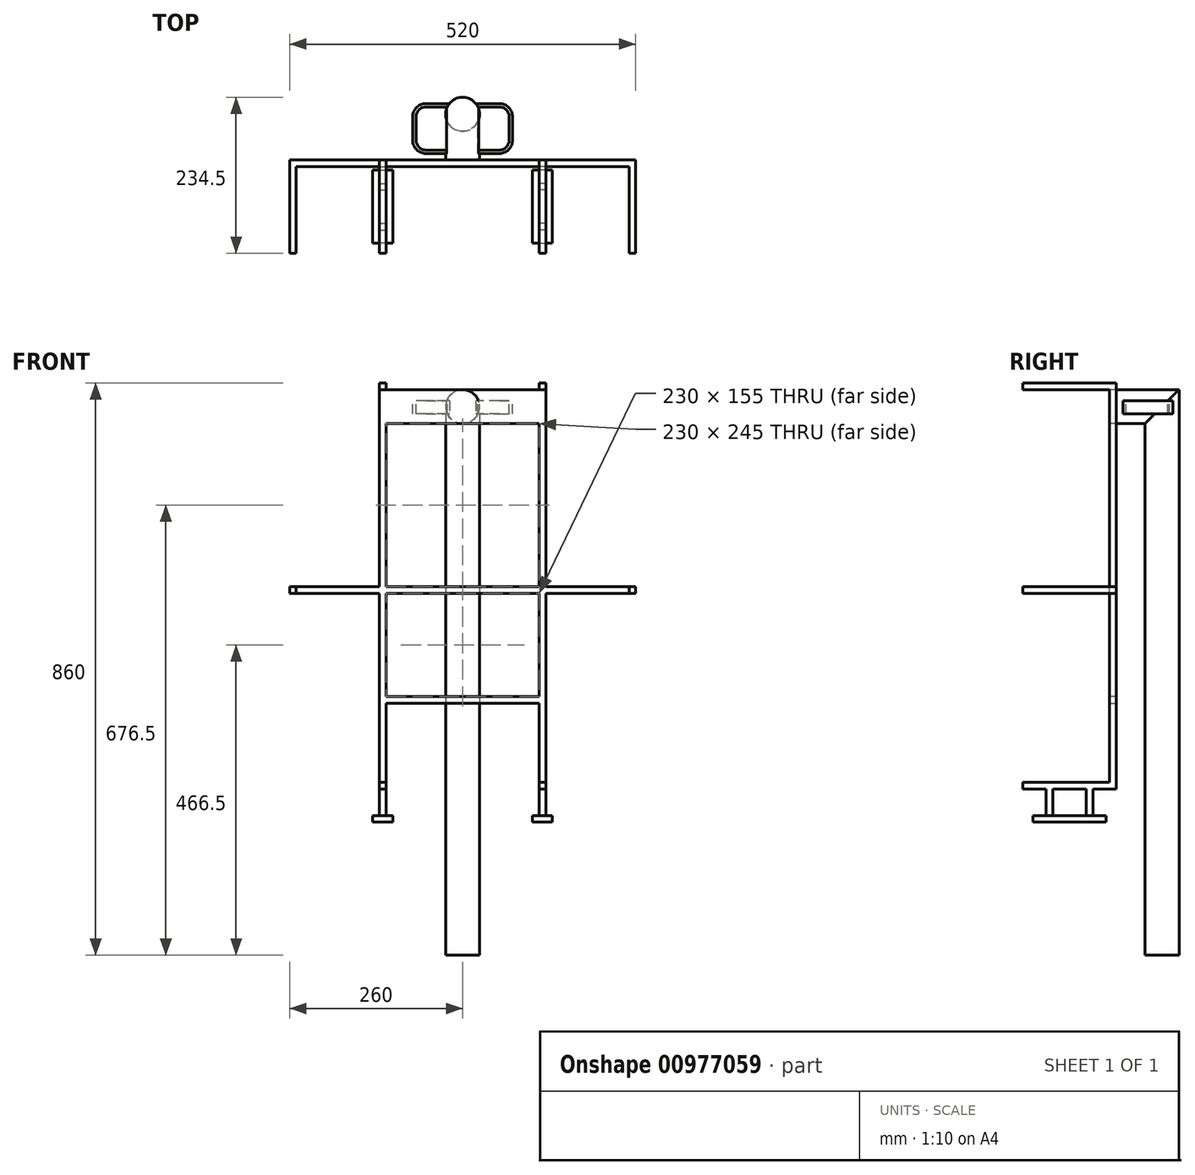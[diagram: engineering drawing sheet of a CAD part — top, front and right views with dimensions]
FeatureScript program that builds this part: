
annotation { "Feature Type Name" : "Feature", "Feature Type Description" : "" }
export const myFeature = defineFeature(function(context is Context, id is Id, definition is map)
    precondition{}
    {
        {
            var Q0;
            Q0=qCreatedBy(makeId("Top.planeOp"),FACE);
            var sketch = newSketch(context, id + "F0", { "sketchPlane" : qUnion([Q0])});
            skCircle(sketch, "E0", {"center": v(0, 0) * mm, "radius": 25.5 * mm});
            skSolve(sketch);
        }
        {
            var Q0;
            Q0=makeQuery(id+"F0.imprint","IMPRINT",FACE,{"disambiguationData":[TD([[makeQuery(id+"F0.imprint","IMPRINT",EDGE,{"derivedFrom":sQuery(id+"F0.wireOp",EDGE,"E0")}),1.0]])]});
            extrude(context, id + "F1", {"entities" : qUnion([Q0]), "depth" : 850 * mm, "offsetDistance" : 25 * mm});
        }
        {
            var Q0;
            Q0=qCreatedBy(makeId("Front.planeOp"),FACE);
            var sketch = newSketch(context, id + "F2", { "sketchPlane" : qUnion([Q0])});
            skCircle(sketch, "E1", {"center": v(0, 824.5) * mm, "radius": 25.5 * mm});
            skSolve(sketch);
        }
        {
            var Q0;
            Q0=makeQuery(id+"F2.imprint","IMPRINT",FACE,{"disambiguationData":[TD([[makeQuery(id+"F2.imprint","IMPRINT",EDGE,{"derivedFrom":sQuery(id+"F2.wireOp",EDGE,"E1")}),1.0]])]});
            extrude(context, id + "F3", {"entities" : qUnion([Q0]), "operationType" : NewBodyOperationType.ADD, "depth" : 69 * mm, "offsetDistance" : 25 * mm});
        }
        {
            var Q0;
            Q0=makeQuery(id+"F3.opExtrude","CAP_FACE",FACE,{"disambiguationData":[OSD([sQuery(id+"F2.wireOp",EDGE,"E1")])],"isStart":false});
            var sketch = newSketch(context, id + "F4", { "sketchPlane" : qUnion([Q0])});
            skArc(sketch, "E2", {"start": v(25.5, 824.5) * mm, "mid": v(0, 850) * mm, "end": v(-25.5, 824.5) * mm});
            skLineSegment(sketch, "E3", {"start": v(-25.5, 824.5) * mm, "end": v(-40.8, 824.5) * mm});
            skLineSegment(sketch, "E4", {"start": v(-40.8, 824.5) * mm, "end": v(-40.8, 859.7) * mm});
            skLineSegment(sketch, "E5", {"start": v(-40.8, 859.7) * mm, "end": v(45.6, 859.7) * mm});
            skLineSegment(sketch, "E6", {"start": v(45.6, 859.7) * mm, "end": v(45.6, 824.5) * mm});
            skLineSegment(sketch, "E7", {"start": v(45.6, 824.5) * mm, "end": v(25.5, 824.5) * mm});
            skSolve(sketch);
        }
        {
            var Q0;
            Q0=makeQuery(id+"F4.imprint","IMPRINT",FACE,{"disambiguationData":[TD([[makeQuery(id+"F4.imprint","IMPRINT",EDGE,{"derivedFrom":sQuery(id+"F4.wireOp",EDGE,"E2")}),-1.0]])]});
            extrude(context, id + "F5", {"entities" : qUnion([Q0]), "operationType" : NewBodyOperationType.REMOVE, "oppositeDirection" : true, "depth" : 150 * mm, "offsetDistance" : 25 * mm});
        }
        {
            var Q0;
            Q0=qCreatedBy(makeId("Right.planeOp"),FACE);
            var sketch = newSketch(context, id + "F6", { "sketchPlane" : qUnion([Q0])});
            skLineSegment(sketch, "E8", {"start": v(-59, 823.42) * mm, "end": v(-59, 833.42) * mm});
            skLineSegment(sketch, "E9", {"start": v(-59, 833.42) * mm, "end": v(16, 833.42) * mm});
            skLineSegment(sketch, "E10", {"start": v(16, 833.42) * mm, "end": v(16, 813.42) * mm});
            skLineSegment(sketch, "E11", {"start": v(16, 813.42) * mm, "end": v(-59, 813.42) * mm});
            skLineSegment(sketch, "E12", {"start": v(-59, 813.42) * mm, "end": v(-59, 823.42) * mm});
            skSolve(sketch);
        }
        {
            var Q0;
            Q0 = qSketchRegion(id + "F6", true);
            extrude(context, id + "F7", {"entities" : qUnion([Q0]), "operationType" : NewBodyOperationType.ADD, "endBound" : BoundingType.SYMMETRIC, "depth" : 150 * mm, "offsetDistance" : 25 * mm});
        }
        {
            var Q0;
            Q0=makeQuery(id+"F7.opExtrude","CAP_EDGE",EDGE,{"disambiguationData":[OSD([sQuery(id+"F6.wireOp",EDGE,"E10")])],"isStart":false});
            var Q1;
            Q1=makeQuery(id+"F7.opExtrude","CAP_EDGE",EDGE,{"disambiguationData":[OSD([sQuery(id+"F6.wireOp",EDGE,"E10")])],"isStart":true});
            var Q2;
            Q2=makeQuery(id+"F7.opExtrude","CAP_EDGE",EDGE,{"disambiguationData":[OSD([sQuery(id+"F6.wireOp",EDGE,"E8"),sQuery(id+"F6.wireOp",EDGE,"E12")])],"isStart":true});
            var Q3;
            Q3=makeQuery(id+"F7.opExtrude","CAP_EDGE",EDGE,{"disambiguationData":[OSD([sQuery(id+"F6.wireOp",EDGE,"E8"),sQuery(id+"F6.wireOp",EDGE,"E12")])],"isStart":false});
            fillet(context, id + "F8", {"entities" : qUnion([Q0, Q1, Q2, Q3]), "radius" : 20 * mm, "tangentPropagation" : true, "allowEdgeOverflow" : false});
        }
        {
            var Q0;
            {var subQ0=sQuery(id+"F6.wireOp",EDGE,"E12");var subQ1=sQuery(id+"F6.wireOp",EDGE,"E10");var subQ2=sQuery(id+"F6.wireOp",EDGE,"E9");var subQ3=sQuery(id+"F6.wireOp",EDGE,"E8");Q0=makeQuery(id+"F7.boolean.opBoolean","SPLIT",FACE,{"disambiguationData":[TD([makeQuery(id+"F7.opExtrude","CAP_FACE",FACE,{"disambiguationData":[OSD([subQ3,subQ2,subQ1,sQuery(id+"F6.wireOp",EDGE,"E11"),subQ0])],"isStart":false})])],"derivedFrom":makeQuery(id+"F7.opExtrude","SWEPT_FACE",FACE,{"disambiguationData":[OSD([subQ2])]})});}
            var sketch = newSketch(context, id + "F9", { "sketchPlane" : qUnion([Q0])});
            skLineSegment(sketch, "E13", {"start": v(23.89, -54) * mm, "end": v(55, -54) * mm});
            skLineSegment(sketch, "E14", {"start": v(55, 11) * mm, "end": v(23, 11) * mm});
            skLineSegment(sketch, "E15", {"start": v(70, -4) * mm, "end": v(70, -39) * mm});
            skArc(sketch, "E16", {"start": v(55, -54) * mm, "mid": v(65.6, -49.6) * mm, "end": v(70, -39) * mm});
            skArc(sketch, "E17", {"start": v(70, -4) * mm, "mid": v(65.6, 6.6) * mm, "end": v(55, 11) * mm});
            skLineSegment(sketch, "E18", {"start": v(23.89, -54) * mm, "end": v(23.89, 8.92) * mm});
            skLineSegment(sketch, "E19", {"start": v(23.89, 8.92) * mm, "end": v(23, 11) * mm});
            skLineSegment(sketch, "E20.MirrorCS", {"start": v(-23.89, 8.92) * mm, "end": v(-23, 11) * mm});
            skLineSegment(sketch, "E21.MirrorCS", {"start": v(-23.89, -54) * mm, "end": v(-23.89, 8.92) * mm});
            skLineSegment(sketch, "E22.MirrorCS", {"start": v(-55, 11) * mm, "end": v(-23, 11) * mm});
            skArc(sketch, "E23.MirrorCS", {"start": v(-70, -4) * mm, "mid": v(-65.6, 6.6) * mm, "end": v(-55, 11) * mm});
            skLineSegment(sketch, "E24.MirrorCS", {"start": v(-23.89, -54) * mm, "end": v(-55, -54) * mm});
            skLineSegment(sketch, "E25.MirrorCS", {"start": v(-70, -4) * mm, "end": v(-70, -39) * mm});
            skArc(sketch, "E26.MirrorCS", {"start": v(-55, -54) * mm, "mid": v(-65.6, -49.6) * mm, "end": v(-70, -39) * mm});
            skSolve(sketch);
        }
        {
            var Q0;
            Q0=makeQuery(id+"F9.imprint","IMPRINT",FACE,{"disambiguationData":[TD([[makeQuery(id+"F9.imprint","IMPRINT",EDGE,{"derivedFrom":sQuery(id+"F9.wireOp",EDGE,"E20.MirrorCS")}),1.0]])]});
            var Q1;
            Q1=makeQuery(id+"F9.imprint","IMPRINT",FACE,{"disambiguationData":[TD([[makeQuery(id+"F9.imprint","IMPRINT",EDGE,{"derivedFrom":sQuery(id+"F9.wireOp",EDGE,"E13")}),1.0]])]});
            extrude(context, id + "F10", {"entities" : qUnion([Q0, Q1]), "operationType" : NewBodyOperationType.REMOVE, "oppositeDirection" : true, "depth" : 20 * mm, "offsetDistance" : 25 * mm});
        }
        {
            var Q0;
            Q0=makeQuery(id+"F3.opExtrude","CAP_FACE",FACE,{"disambiguationData":[OSD([sQuery(id+"F2.wireOp",EDGE,"E1")])],"isStart":false});
            var sketch = newSketch(context, id + "F11", { "sketchPlane" : qUnion([Q0])});
            skLineSegment(sketch, "E27", {"start": v(125, 850) * mm, "end": v(125, 554) * mm});
            skLineSegment(sketch, "E28", {"start": v(125, 250) * mm, "end": v(115, 250) * mm});
            skLineSegment(sketch, "E29", {"start": v(260, 544) * mm, "end": v(260, 554) * mm});
            skLineSegment(sketch, "E30", {"start": v(260, 554) * mm, "end": v(125, 554) * mm});
            skLineSegment(sketch, "E31.trimOffspring", {"start": v(125, 544) * mm, "end": v(125, 250) * mm});
            skLineSegment(sketch, "E32.trimOffspring", {"start": v(125, 544) * mm, "end": v(260, 544) * mm});
            skLineSegment(sketch, "E33", {"start": v(0, 379) * mm, "end": v(115, 379) * mm});
            skLineSegment(sketch, "E34.trimOffspring", {"start": v(115, 379) * mm, "end": v(115, 250) * mm});
            skLineSegment(sketch, "E35.MirrorCS", {"start": v(-125, 250) * mm, "end": v(-115, 250) * mm});
            skLineSegment(sketch, "E36.MirrorCS", {"start": v(0, 379) * mm, "end": v(-115, 379) * mm});
            skLineSegment(sketch, "E37.MirrorCS", {"start": v(-115, 379) * mm, "end": v(-115, 250) * mm});
            skLineSegment(sketch, "E38.MirrorCS", {"start": v(-260, 544) * mm, "end": v(-260, 554) * mm});
            skLineSegment(sketch, "E39.MirrorCS", {"start": v(-125, 544) * mm, "end": v(-125, 250) * mm});
            skLineSegment(sketch, "E40.MirrorCS", {"start": v(-260, 554) * mm, "end": v(-125, 554) * mm});
            skLineSegment(sketch, "E41.MirrorCS", {"start": v(-125, 544) * mm, "end": v(-260, 544) * mm});
            skLineSegment(sketch, "E42.MirrorCS", {"start": v(-125, 850) * mm, "end": v(-125, 554) * mm});
            skLineSegment(sketch, "E43", {"start": v(-125, 850) * mm, "end": v(125, 850) * mm});
            skSolve(sketch);
        }
        {
            var Q0;
            Q0 = qSketchRegion(id + "F11", true);
            extrude(context, id + "F12", {"entities" : qUnion([Q0]), "depth" : 10 * mm, "offsetDistance" : 25 * mm});
        }
        {
            var Q0;
            Q0=makeQuery(id+"F12.opExtrude","CAP_FACE",FACE,{"disambiguationData":[OSD([sQuery(id+"F11.wireOp",EDGE,"E27"),sQuery(id+"F11.wireOp",EDGE,"E28"),sQuery(id+"F11.wireOp",EDGE,"E29"),sQuery(id+"F11.wireOp",EDGE,"E30"),sQuery(id+"F11.wireOp",EDGE,"E31.trimOffspring"),sQuery(id+"F11.wireOp",EDGE,"E32.trimOffspring"),sQuery(id+"F11.wireOp",EDGE,"E33"),sQuery(id+"F11.wireOp",EDGE,"E34.trimOffspring"),sQuery(id+"F11.wireOp",EDGE,"E35.MirrorCS"),sQuery(id+"F11.wireOp",EDGE,"E36.MirrorCS"),sQuery(id+"F11.wireOp",EDGE,"E37.MirrorCS"),sQuery(id+"F11.wireOp",EDGE,"E38.MirrorCS"),sQuery(id+"F11.wireOp",EDGE,"E39.MirrorCS"),sQuery(id+"F11.wireOp",EDGE,"E40.MirrorCS"),sQuery(id+"F11.wireOp",EDGE,"E41.MirrorCS"),sQuery(id+"F11.wireOp",EDGE,"E42.MirrorCS"),sQuery(id+"F11.wireOp",EDGE,"E43")])],"isStart":false});
            var sketch = newSketch(context, id + "F13", { "sketchPlane" : qUnion([Q0])});
            skLineSegment(sketch, "E44", {"start": v(0, 799) * mm, "end": v(115, 799) * mm});
            skLineSegment(sketch, "E45", {"start": v(115, 799) * mm, "end": v(115, 554) * mm});
            skLineSegment(sketch, "E46", {"start": v(0, 799) * mm, "end": v(-115, 799) * mm});
            skLineSegment(sketch, "E47", {"start": v(-115, 799) * mm, "end": v(-115, 554) * mm});
            skLineSegment(sketch, "E48", {"start": v(-115, 554) * mm, "end": v(115, 554) * mm});
            skLineSegment(sketch, "E49", {"start": v(-115, 544) * mm, "end": v(115, 544) * mm});
            skLineSegment(sketch, "E50", {"start": v(115, 544) * mm, "end": v(115, 389) * mm});
            skLineSegment(sketch, "E51", {"start": v(115, 389) * mm, "end": v(-115, 389) * mm});
            skLineSegment(sketch, "E52", {"start": v(-115, 389) * mm, "end": v(-115, 544) * mm});
            skSolve(sketch);
        }
        {
            var Q0;
            Q0=makeQuery(id+"F13.imprint","IMPRINT",FACE,{"disambiguationData":[TD([[makeQuery(id+"F13.imprint","IMPRINT",EDGE,{"derivedFrom":sQuery(id+"F13.wireOp",EDGE,"E44")}),-1.0]])]});
            var Q1;
            Q1=makeQuery(id+"F13.imprint","IMPRINT",FACE,{"disambiguationData":[TD([[makeQuery(id+"F13.imprint","IMPRINT",EDGE,{"derivedFrom":sQuery(id+"F13.wireOp",EDGE,"E49")}),-1.0]])]});
            extrude(context, id + "F14", {"entities" : qUnion([Q0, Q1]), "operationType" : NewBodyOperationType.REMOVE, "oppositeDirection" : true, "depth" : 10 * mm, "offsetDistance" : 25 * mm});
        }
        {
            var Q0;
            Q0=makeQuery(id+"F12.opExtrude","CAP_FACE",FACE,{"disambiguationData":[OSD([sQuery(id+"F11.wireOp",EDGE,"E27"),sQuery(id+"F11.wireOp",EDGE,"E28"),sQuery(id+"F11.wireOp",EDGE,"E29"),sQuery(id+"F11.wireOp",EDGE,"E30"),sQuery(id+"F11.wireOp",EDGE,"E31.trimOffspring"),sQuery(id+"F11.wireOp",EDGE,"E32.trimOffspring"),sQuery(id+"F11.wireOp",EDGE,"E33"),sQuery(id+"F11.wireOp",EDGE,"E34.trimOffspring"),sQuery(id+"F11.wireOp",EDGE,"E35.MirrorCS"),sQuery(id+"F11.wireOp",EDGE,"E36.MirrorCS"),sQuery(id+"F11.wireOp",EDGE,"E37.MirrorCS"),sQuery(id+"F11.wireOp",EDGE,"E38.MirrorCS"),sQuery(id+"F11.wireOp",EDGE,"E39.MirrorCS"),sQuery(id+"F11.wireOp",EDGE,"E40.MirrorCS"),sQuery(id+"F11.wireOp",EDGE,"E41.MirrorCS"),sQuery(id+"F11.wireOp",EDGE,"E42.MirrorCS"),sQuery(id+"F11.wireOp",EDGE,"E43")])],"isStart":false});
            var sketch = newSketch(context, id + "F15", { "sketchPlane" : qUnion([Q0])});
            skLineSegment(sketch, "E53.bottom", {"start": v(-260, 554) * mm, "end": v(-250, 554) * mm});
            skLineSegment(sketch, "E53.top", {"start": v(-260, 544) * mm, "end": v(-250, 544) * mm});
            skLineSegment(sketch, "E53.left", {"start": v(-260, 554) * mm, "end": v(-260, 544) * mm});
            skLineSegment(sketch, "E53.right", {"start": v(-250, 554) * mm, "end": v(-250, 544) * mm});
            skLineSegment(sketch, "E54.bottom", {"start": v(260, 544) * mm, "end": v(250, 544) * mm});
            skLineSegment(sketch, "E54.top", {"start": v(260, 554) * mm, "end": v(250, 554) * mm});
            skLineSegment(sketch, "E54.left", {"start": v(260, 544) * mm, "end": v(260, 554) * mm});
            skLineSegment(sketch, "E54.right", {"start": v(250, 544) * mm, "end": v(250, 554) * mm});
            skLineSegment(sketch, "E55.bottom", {"start": v(-115, 250) * mm, "end": v(-125, 250) * mm});
            skLineSegment(sketch, "E55.top", {"start": v(-115, 260) * mm, "end": v(-125, 260) * mm});
            skLineSegment(sketch, "E55.left", {"start": v(-115, 250) * mm, "end": v(-115, 260) * mm});
            skLineSegment(sketch, "E55.right", {"start": v(-125, 250) * mm, "end": v(-125, 260) * mm});
            skLineSegment(sketch, "E56.bottom", {"start": v(125, 250) * mm, "end": v(115, 250) * mm});
            skLineSegment(sketch, "E56.top", {"start": v(125, 260) * mm, "end": v(115, 260) * mm});
            skLineSegment(sketch, "E56.left", {"start": v(125, 250) * mm, "end": v(125, 260) * mm});
            skLineSegment(sketch, "E56.right", {"start": v(115, 250) * mm, "end": v(115, 260) * mm});
            skSolve(sketch);
        }
        {
            var Q0;
            Q0=makeQuery(id+"F12.opExtrude","SWEPT_FACE",FACE,{"disambiguationData":[OSD([sQuery(id+"F11.wireOp",EDGE,"E43")])]});
            var sketch = newSketch(context, id + "F16", { "sketchPlane" : qUnion([Q0])});
            skLineSegment(sketch, "E57.bottom", {"start": v(-125, -69) * mm, "end": v(-115, -69) * mm});
            skLineSegment(sketch, "E57.top", {"start": v(-125, -209) * mm, "end": v(-115, -209) * mm});
            skLineSegment(sketch, "E57.left", {"start": v(-125, -69) * mm, "end": v(-125, -209) * mm});
            skLineSegment(sketch, "E57.right", {"start": v(-115, -69) * mm, "end": v(-115, -209) * mm});
            skLineSegment(sketch, "E58.bottom", {"start": v(125, -69) * mm, "end": v(115, -69) * mm});
            skLineSegment(sketch, "E58.top", {"start": v(125, -209) * mm, "end": v(115, -209) * mm});
            skLineSegment(sketch, "E58.left", {"start": v(125, -69) * mm, "end": v(125, -209) * mm});
            skLineSegment(sketch, "E58.right", {"start": v(115, -69) * mm, "end": v(115, -209) * mm});
            skSolve(sketch);
        }
        {
            var Q0;
            {var subQ0=sQuery(id+"F16.wireOp",EDGE,"E57.top");Q0=makeQuery(id+"F16.imprint","IMPRINT",FACE,{"disambiguationData":[TD([[makeQuery(id+"F16.imprint","IMPRINT",EDGE,{"derivedFrom":subQ0}),1.0]])]});}
            var Q1;
            {var subQ0=sQuery(id+"F16.wireOp",EDGE,"E58.bottom");Q1=makeQuery(id+"F16.imprint","IMPRINT",FACE,{"disambiguationData":[TD([[makeQuery(id+"F16.imprint","IMPRINT",EDGE,{"derivedFrom":subQ0}),-1.0]])]});}
            var Q2;
            {var subQ0=sQuery(id+"F16.wireOp",EDGE,"E57.bottom");Q2=makeQuery(id+"F16.imprint","IMPRINT",FACE,{"disambiguationData":[TD([[makeQuery(id+"F16.imprint","IMPRINT",EDGE,{"derivedFrom":subQ0}),-1.0]])]});}
            var Q3;
            {var subQ0=sQuery(id+"F16.wireOp",EDGE,"E58.top");Q3=makeQuery(id+"F16.imprint","IMPRINT",FACE,{"disambiguationData":[TD([[makeQuery(id+"F16.imprint","IMPRINT",EDGE,{"derivedFrom":subQ0}),-1.0]])]});}
            extrude(context, id + "F17", {"entities" : qUnion([Q0, Q1, Q2, Q3]), "operationType" : NewBodyOperationType.ADD, "depth" : 10 * mm, "offsetDistance" : 25 * mm});
        }
        {
            var Q0;
            Q0=makeQuery(id+"F15.imprint","IMPRINT",FACE,{"disambiguationData":[TD([[makeQuery(id+"F15.imprint","IMPRINT",EDGE,{"derivedFrom":sQuery(id+"F15.wireOp",EDGE,"E53.bottom")}),-1.0]])]});
            var Q1;
            Q1=makeQuery(id+"F15.imprint","IMPRINT",FACE,{"disambiguationData":[TD([[makeQuery(id+"F15.imprint","IMPRINT",EDGE,{"derivedFrom":sQuery(id+"F15.wireOp",EDGE,"E54.bottom")}),1.0]])]});
            var Q2;
            Q2=makeQuery(id+"F15.imprint","IMPRINT",FACE,{"disambiguationData":[TD([[makeQuery(id+"F15.imprint","IMPRINT",EDGE,{"derivedFrom":sQuery(id+"F15.wireOp",EDGE,"E56.bottom")}),-1.0]])]});
            var Q3;
            Q3=makeQuery(id+"F15.imprint","IMPRINT",FACE,{"disambiguationData":[TD([[makeQuery(id+"F15.imprint","IMPRINT",EDGE,{"derivedFrom":sQuery(id+"F15.wireOp",EDGE,"E55.bottom")}),1.0]])]});
            extrude(context, id + "F18", {"entities" : qUnion([Q0, Q1, Q2, Q3]), "operationType" : NewBodyOperationType.ADD, "depth" : 130 * mm, "offsetDistance" : 25 * mm});
        }
        {
            var Q0;
            Q0=makeQuery(id+"F18.boolean.opBoolean","MERGE",FACE,{"derivedFrom":[makeQuery(id+"F12.opExtrude","SWEPT_FACE",FACE,{"disambiguationData":[OSD([sQuery(id+"F11.wireOp",EDGE,"E35.MirrorCS")])]}),makeQuery(id+"F18.opExtrude","SWEPT_FACE",FACE,{"disambiguationData":[OSD([sQuery(id+"F15.wireOp",EDGE,"E55.bottom")])]})]});
            var sketch = newSketch(context, id + "F19", { "sketchPlane" : qUnion([Q0])});
            skLineSegment(sketch, "E59.bottom", {"start": v(-125, 174) * mm, "end": v(-115, 174) * mm});
            skLineSegment(sketch, "E59.top", {"start": v(-125, 164) * mm, "end": v(-115, 164) * mm});
            skLineSegment(sketch, "E59.left", {"start": v(-125, 174) * mm, "end": v(-125, 164) * mm});
            skLineSegment(sketch, "E59.right", {"start": v(-115, 174) * mm, "end": v(-115, 164) * mm});
            skLineSegment(sketch, "E60.bottom", {"start": v(-125, 114) * mm, "end": v(-115, 114) * mm});
            skLineSegment(sketch, "E60.top", {"start": v(-125, 104) * mm, "end": v(-115, 104) * mm});
            skLineSegment(sketch, "E60.left", {"start": v(-125, 114) * mm, "end": v(-125, 104) * mm});
            skLineSegment(sketch, "E60.right", {"start": v(-115, 114) * mm, "end": v(-115, 104) * mm});
            skLineSegment(sketch, "E61.MirrorCS", {"start": v(125, 174) * mm, "end": v(125, 164) * mm});
            skLineSegment(sketch, "E62.MirrorCS", {"start": v(115, 174) * mm, "end": v(115, 164) * mm});
            skLineSegment(sketch, "E63.MirrorCS", {"start": v(125, 174) * mm, "end": v(115, 174) * mm});
            skLineSegment(sketch, "E64.MirrorCS", {"start": v(125, 164) * mm, "end": v(115, 164) * mm});
            skLineSegment(sketch, "E65.MirrorCS", {"start": v(125, 114) * mm, "end": v(115, 114) * mm});
            skLineSegment(sketch, "E66.MirrorCS", {"start": v(115, 114) * mm, "end": v(115, 104) * mm});
            skLineSegment(sketch, "E67.MirrorCS", {"start": v(125, 104) * mm, "end": v(115, 104) * mm});
            skLineSegment(sketch, "E68.MirrorCS", {"start": v(125, 114) * mm, "end": v(125, 104) * mm});
            skSolve(sketch);
        }
        {
            var Q0;
            Q0=makeQuery(id+"F19.imprint","IMPRINT",FACE,{"disambiguationData":[TD([[makeQuery(id+"F19.imprint","IMPRINT",EDGE,{"derivedFrom":sQuery(id+"F19.wireOp",EDGE,"E60.bottom")}),-1.0]])]});
            var Q1;
            Q1=makeQuery(id+"F19.imprint","IMPRINT",FACE,{"disambiguationData":[TD([[makeQuery(id+"F19.imprint","IMPRINT",EDGE,{"derivedFrom":sQuery(id+"F19.wireOp",EDGE,"E59.bottom")}),-1.0]])]});
            var Q2;
            Q2=makeQuery(id+"F19.imprint","IMPRINT",FACE,{"disambiguationData":[TD([[makeQuery(id+"F19.imprint","IMPRINT",EDGE,{"derivedFrom":sQuery(id+"F19.wireOp",EDGE,"E61.MirrorCS")}),-1.0]])]});
            var Q3;
            Q3=makeQuery(id+"F19.imprint","IMPRINT",FACE,{"disambiguationData":[TD([[makeQuery(id+"F19.imprint","IMPRINT",EDGE,{"derivedFrom":sQuery(id+"F19.wireOp",EDGE,"E65.MirrorCS")}),1.0]])]});
            extrude(context, id + "F20", {"entities" : qUnion([Q0, Q1, Q2, Q3]), "operationType" : NewBodyOperationType.ADD, "depth" : 40 * mm, "offsetDistance" : 25 * mm});
        }
        {
            var Q0;
            Q0=makeQuery(id+"F20.opExtrude","CAP_FACE",FACE,{"disambiguationData":[OSD([sQuery(id+"F19.wireOp",EDGE,"E60.bottom"),sQuery(id+"F19.wireOp",EDGE,"E60.top"),sQuery(id+"F19.wireOp",EDGE,"E60.left"),sQuery(id+"F19.wireOp",EDGE,"E60.right")])],"isStart":false});
            var sketch = newSketch(context, id + "F21", { "sketchPlane" : qUnion([Q0])});
            skLineSegment(sketch, "E69", {"start": v(-135, 104) * mm, "end": v(-135, 84) * mm});
            skLineSegment(sketch, "E70", {"start": v(-135, 84) * mm, "end": v(-105, 84) * mm});
            skLineSegment(sketch, "E71", {"start": v(-105, 84) * mm, "end": v(-105, 194) * mm});
            skLineSegment(sketch, "E72", {"start": v(-105, 194) * mm, "end": v(-135, 194) * mm});
            skLineSegment(sketch, "E73", {"start": v(-135, 194) * mm, "end": v(-135, 104) * mm});
            skLineSegment(sketch, "E74.MirrorCS", {"start": v(135, 84) * mm, "end": v(105, 84) * mm});
            skLineSegment(sketch, "E75.MirrorCS", {"start": v(135, 104) * mm, "end": v(135, 84) * mm});
            skLineSegment(sketch, "E76.MirrorCS", {"start": v(135, 194) * mm, "end": v(135, 104) * mm});
            skLineSegment(sketch, "E77.MirrorCS", {"start": v(105, 84) * mm, "end": v(105, 194) * mm});
            skLineSegment(sketch, "E78.MirrorCS", {"start": v(105, 194) * mm, "end": v(135, 194) * mm});
            skSolve(sketch);
        }
        {
            var Q0;
            Q0=makeQuery(id+"F21.imprint","IMPRINT",FACE,{"disambiguationData":[TD([[makeQuery(id+"F21.imprint","IMPRINT",EDGE,{"derivedFrom":sQuery(id+"F21.wireOp",EDGE,"E69")}),1.0]])]});
            var Q1;
            Q1=makeQuery(id+"F21.imprint","IMPRINT",FACE,{"disambiguationData":[TD([[makeQuery(id+"F21.imprint","IMPRINT",EDGE,{"derivedFrom":sQuery(id+"F21.wireOp",EDGE,"E74.MirrorCS")}),-1.0]])]});
            var Q2;
            Q2=makeQuery(id+"F21.imprint","IMPRINT",FACE,{"disambiguationData":[TD([[makeQuery(id+"F21.imprint","IMPRINT",EDGE,{"derivedFrom":makeQuery(id+"F20.opExtrude","CAP_EDGE",EDGE,{"disambiguationData":[OSD([sQuery(id+"F19.wireOp",EDGE,"E60.bottom")])],"isStart":false})}),-1.0]])]});
            extrude(context, id + "F22", {"entities" : qUnion([Q0, Q1, Q2]), "operationType" : NewBodyOperationType.ADD, "depth" : 10 * mm, "offsetDistance" : 25 * mm});
        }
    });
